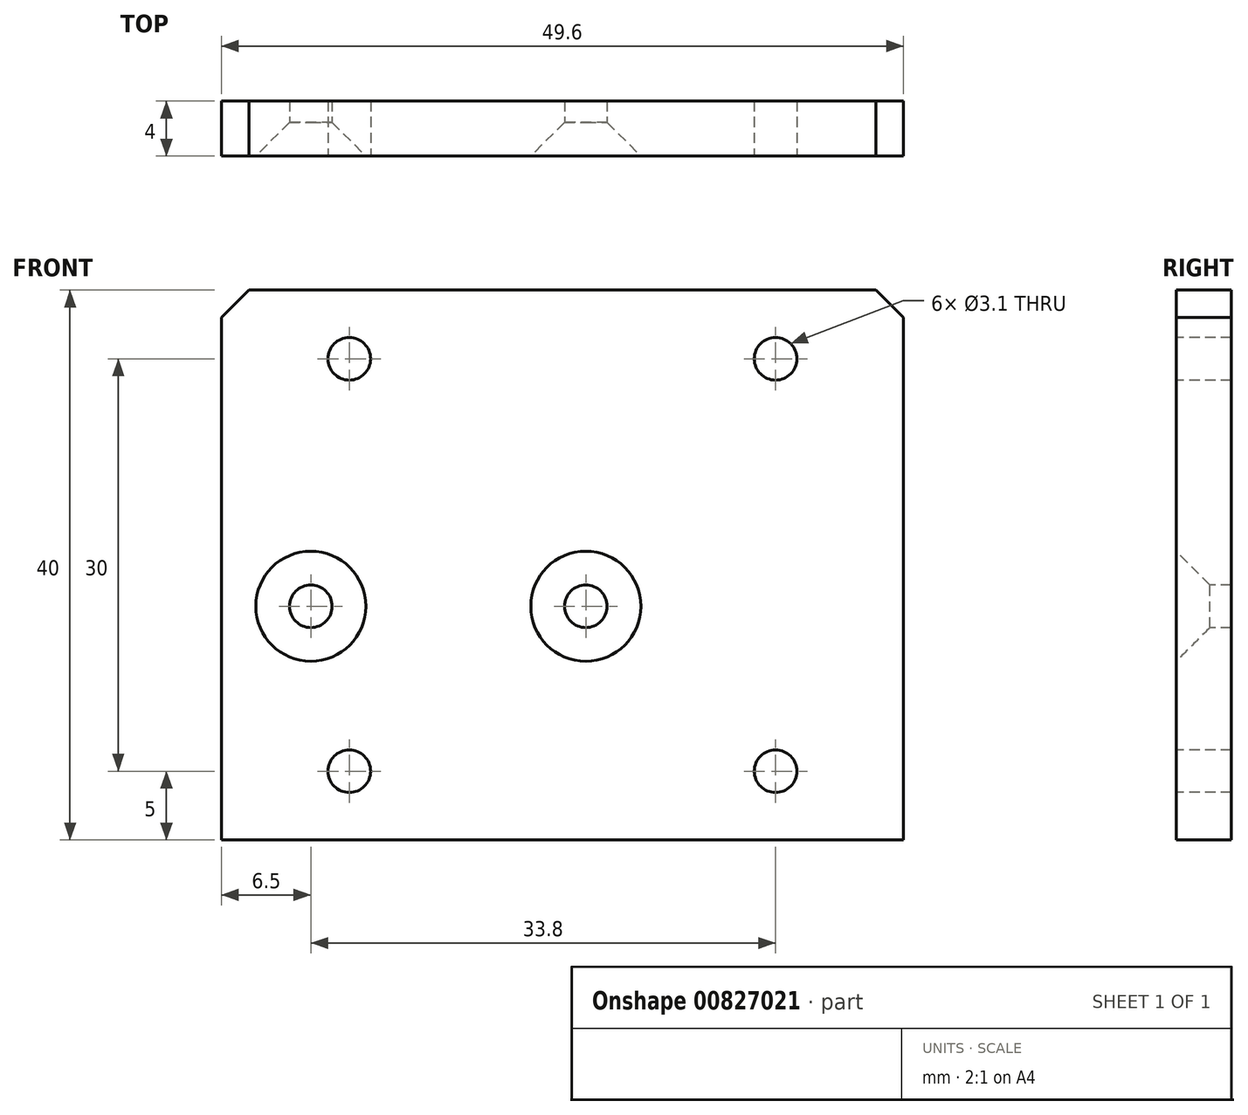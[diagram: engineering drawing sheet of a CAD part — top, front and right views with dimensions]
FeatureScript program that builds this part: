
annotation { "Feature Type Name" : "Feature", "Feature Type Description" : "" }
export const myFeature = defineFeature(function(context is Context, id is Id, definition is map)
    precondition{}
    {
        {
            var Q0;
            Q0=qCreatedBy(makeId("Front.planeOp"),FACE);
            var sketch = newSketch(context, id + "F0", { "sketchPlane" : qUnion([Q0])});
            skLineSegment(sketch, "E0.bottom", {"start": v(0, 0) * mm, "end": v(49.6, 0) * mm});
            skLineSegment(sketch, "E0.top", {"start": v(0, 60) * mm, "end": v(49.6, 60) * mm});
            skLineSegment(sketch, "E0.left", {"start": v(0, 0) * mm, "end": v(0, 60) * mm});
            skLineSegment(sketch, "E0.right", {"start": v(49.6, 0) * mm, "end": v(49.6, 60) * mm});
            skLineSegment(sketch, "E1", {"start": v(24.8, 60) * mm, "end": v(24.8, 0) * mm, "construction": true});
            skLineSegment(sketch, "E2", {"start": v(9.3, 60) * mm, "end": v(9.3, 0) * mm, "construction": true});
            skLineSegment(sketch, "E3", {"start": v(40.3, 60) * mm, "end": v(40.3, 0) * mm, "construction": true});
            skLineSegment(sketch, "E4", {"start": v(0, 55) * mm, "end": v(49.6, 55) * mm, "construction": true});
            skLineSegment(sketch, "E5", {"start": v(0, 25) * mm, "end": v(49.6, 25) * mm, "construction": true});
            skLineSegment(sketch, "E6.left", {"start": v(0, 34.98) * mm, "end": v(0, 24.98) * mm});
            skPoint(sketch, "E7", {"position": v(6.5, 37) * mm});
            skPoint(sketch, "E8", {"position": v(26.5, 37) * mm});
            skPoint(sketch, "E9", {"position": v(40.3, 25) * mm});
            skPoint(sketch, "E10", {"position": v(9.3, 25) * mm});
            skPoint(sketch, "E11", {"position": v(9.3, 55) * mm});
            skPoint(sketch, "E12", {"position": v(40.3, 55) * mm});
            skLineSegment(sketch, "E13.0", {"start": v(6.5, 25) * mm, "end": v(26.5, 25) * mm});
            skSolve(sketch);
        }
        {
            var Q0;
            {var subQ3=sQuery(id+"F0.wireOp",EDGE,"E0.bottom");Q0=makeQuery(id+"F0.imprint","IMPRINT",FACE,{"disambiguationData":[TD([[makeQuery(id+"F0.imprint","IMPRINT",EDGE,{"derivedFrom":subQ3}),1.0]])]});}
            extrude(context, id + "F1", {"entities" : qUnion([Q0]), "oppositeDirection" : true, "depth" : 4 * mm, "offsetDistance" : 25 * mm});
        }
        {
            var Q0;
            Q0=sQuery(id+"F0.wireOp",VERTEX,"E11");
            var Q1;
            Q1=sQuery(id+"F0.wireOp",VERTEX,"E12");
            var Q2;
            Q2=sQuery(id+"F0.wireOp",VERTEX,"E10");
            var Q3;
            Q3=sQuery(id+"F0.wireOp",VERTEX,"E9");
            var Q4;
            Q4=makeQuery(id+"F1.opExtrude","SWEPT_BODY",BODY,{"disambiguationData":[OSD([sQuery(id+"F0.wireOp",EDGE,"E0.bottom"),sQuery(id+"F0.wireOp",EDGE,"E0.top"),sQuery(id+"F0.wireOp",EDGE,"E0.left"),sQuery(id+"F0.wireOp",EDGE,"E0.right"),sQuery(id+"F0.wireOp",EDGE,"E6.left")])]});
            hole(context, id + "F2", {"style" : HoleStyle.SIMPLE, "endStyle" : HoleEndStyle.THROUGH, "holeDiameter" : 3.1 * mm, "majorDiameter" : 5 * mm, "isTappedThrough" : true, "tappedDepth" : 12 * mm, "tapClearance" : 3, "startFromSketch" : true, "locations" : qUnion([Q0, Q1, Q2, Q3]), "scope" : qUnion([Q4])});
        }
        {
            var Q0;
            Q0=sQuery(id+"F0.wireOp",VERTEX,"E7");
            var Q1;
            Q1=sQuery(id+"F0.wireOp",VERTEX,"E8");
            var Q2;
            Q2=makeQuery(id+"F1.opExtrude","SWEPT_BODY",BODY,{"disambiguationData":[OSD([sQuery(id+"F0.wireOp",EDGE,"E0.bottom"),sQuery(id+"F0.wireOp",EDGE,"E0.top"),sQuery(id+"F0.wireOp",EDGE,"E0.left"),sQuery(id+"F0.wireOp",EDGE,"E0.right"),sQuery(id+"F0.wireOp",EDGE,"E6.left")])]});
            hole(context, id + "F3", {"style" : HoleStyle.C_SINK, "endStyle" : HoleEndStyle.THROUGH, "holeDiameter" : 3.1 * mm, "cSinkDiameter" : 8 * mm, "cSinkAngle" : 90 * degree, "majorDiameter" : 5 * mm, "isTappedThrough" : true, "tappedDepth" : 12 * mm, "tapClearance" : 3, "startFromSketch" : true, "locations" : qUnion([Q0, Q1]), "scope" : qUnion([Q2])});
        }
        {
            var Q0;
            {var subQ3=sQuery(id+"F0.wireOp",EDGE,"E0.bottom");Q0=makeQuery(id+"F0.imprint","IMPRINT",FACE,{"disambiguationData":[TD([[makeQuery(id+"F0.imprint","IMPRINT",EDGE,{"derivedFrom":subQ3}),1.0]])]});}
            var sketch = newSketch(context, id + "F4", { "sketchPlane" : qUnion([Q0])});
            skLineSegment(sketch, "E14.bottom", {"start": v(0, 0) * mm, "end": v(49.6, 0) * mm});
            skLineSegment(sketch, "E14.top", {"start": v(0, 20) * mm, "end": v(49.6, 20) * mm});
            skLineSegment(sketch, "E14.left", {"start": v(0, 0) * mm, "end": v(0, 20) * mm});
            skLineSegment(sketch, "E14.right", {"start": v(49.6, 0) * mm, "end": v(49.6, 20) * mm});
            skSolve(sketch);
        }
        {
            var Q0;
            Q0=qSketchRegion(id+"F4",true);
            extrude(context, id + "F5", {"entities" : qUnion([Q0]), "operationType" : NewBodyOperationType.REMOVE, "endBound" : BoundingType.UP_TO_NEXT, "oppositeDirection" : true, "depth" : 25 * mm, "offsetDistance" : 25 * mm});
        }
        {
            var Q0;
            Q0=makeQuery(id+"F1.opExtrude","SWEPT_EDGE",EDGE,{"disambiguationData":[OSD([sQuery(id+"F0.wireOp",EDGE,"E0.top"),sQuery(id+"F0.wireOp",EDGE,"E0.right")])]});
            var Q1;
            Q1=makeQuery(id+"F5.boolean.opBoolean","COPY",EDGE,{"derivedFrom":makeQuery(id+"F5.opExtrude","SWEPT_EDGE",EDGE,{"disambiguationData":[OSD([sQuery(id+"F0.wireOp",EDGE,"E0.right"),sQuery(id+"F4.wireOp",EDGE,"E14.top"),sQuery(id+"F4.wireOp",EDGE,"E14.right")])]})});
            var Q2;
            Q2=makeQuery(id+"F1.opExtrude","SWEPT_EDGE",EDGE,{"disambiguationData":[OSD([sQuery(id+"F0.wireOp",EDGE,"E0.top"),sQuery(id+"F0.wireOp",EDGE,"E0.left")])]});
            var Q3;
            Q3=makeQuery(id+"F5.boolean.opBoolean","COPY",EDGE,{"derivedFrom":makeQuery(id+"F5.opExtrude","SWEPT_EDGE",EDGE,{"disambiguationData":[OSD([sQuery(id+"F0.wireOp",EDGE,"E0.left"),sQuery(id+"F4.wireOp",EDGE,"E14.top"),sQuery(id+"F4.wireOp",EDGE,"E14.left")])]})});
            chamfer(context, id + "F6", {"entities" : qUnion([Q0, Q1, Q2, Q3]), "width" : 2 * mm, "tangentPropagation" : true});
        }
    });
